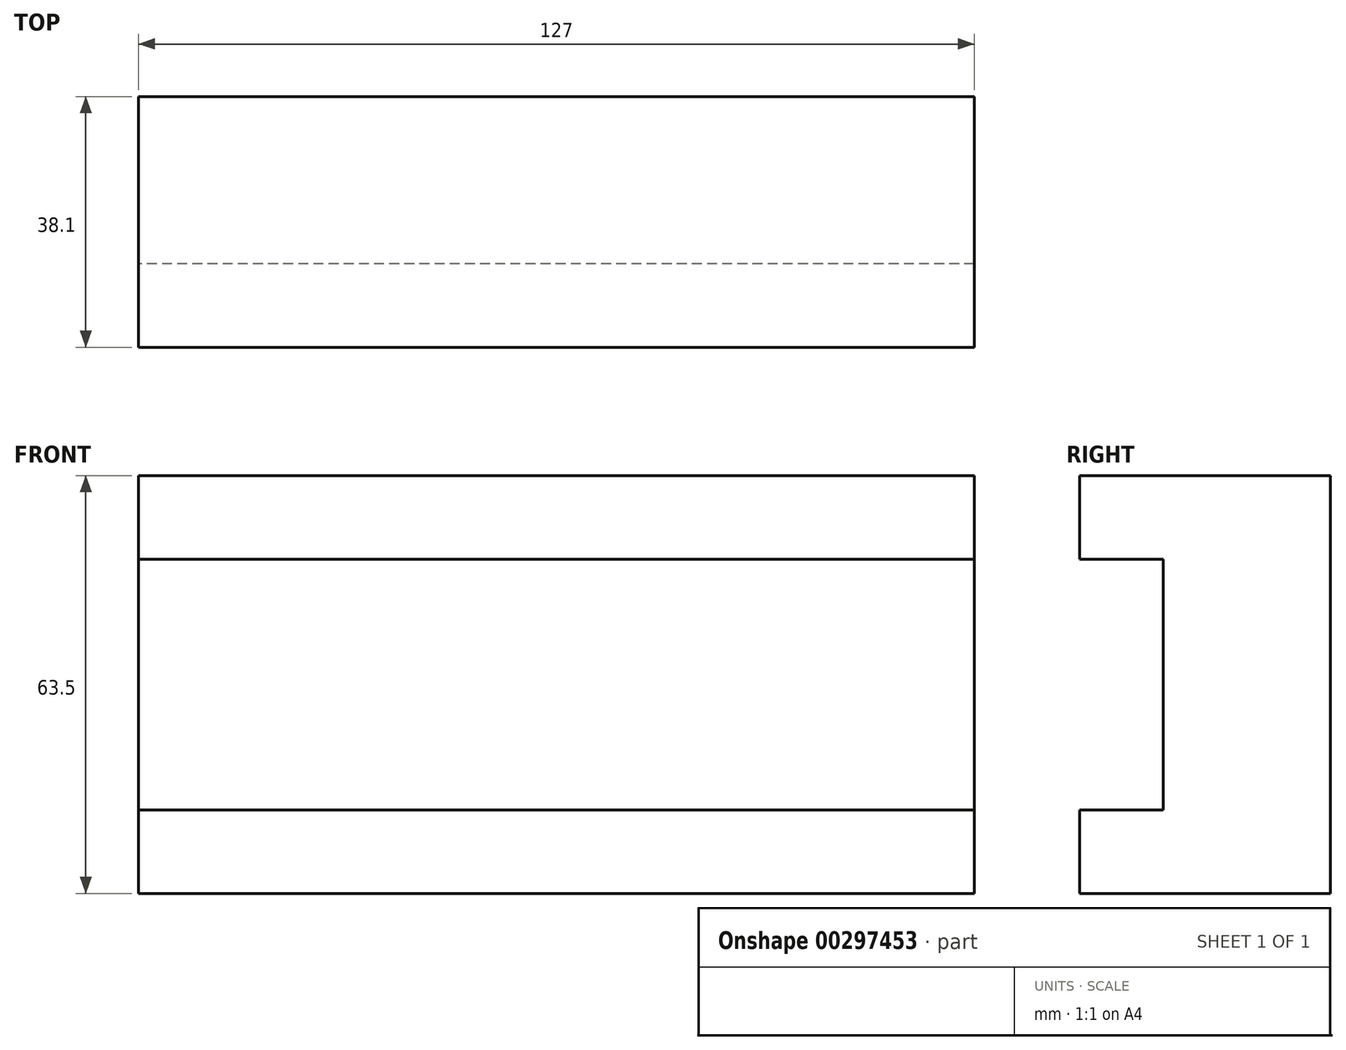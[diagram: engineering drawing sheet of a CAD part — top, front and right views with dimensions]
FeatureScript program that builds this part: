
annotation { "Feature Type Name" : "Feature", "Feature Type Description" : "" }
export const myFeature = defineFeature(function(context is Context, id is Id, definition is map)
    precondition{}
    {
        {
            var Q0;
            Q0=qCreatedBy(makeId("Front.planeOp"),FACE);
            var sketch = newSketch(context, id + "F0", { "sketchPlane" : qUnion([Q0])});
            skLineSegment(sketch, "E0.bottom", {"start": v(63.5, 31.75) * mm, "end": v(-63.5, 31.75) * mm});
            skLineSegment(sketch, "E0.top", {"start": v(63.5, -31.75) * mm, "end": v(-63.5, -31.75) * mm});
            skLineSegment(sketch, "E0.left", {"start": v(63.5, 31.75) * mm, "end": v(63.5, -31.75) * mm});
            skLineSegment(sketch, "E0.right", {"start": v(-63.5, 31.75) * mm, "end": v(-63.5, -31.75) * mm});
            skPoint(sketch, "E0.middle", {"position": v(0, 0) * mm});
            skSolve(sketch);
        }
        {
            var Q0;
            Q0=makeQuery(id+"F0.imprint","IMPRINT",FACE,{"disambiguationData":[TD([[makeQuery(id+"F0.imprint","IMPRINT",EDGE,{"derivedFrom":sQuery(id+"F0.wireOp",EDGE,"E0.bottom")}),1.0]])]});
            extrude(context, id + "F1", {"entities" : qUnion([Q0]), "depth" : 38.1 * mm});
        }
        {
            var Q0;
            Q0=makeQuery(id+"F1.opExtrude","CAP_FACE",FACE,{"disambiguationData":[OSD([sQuery(id+"F0.wireOp",EDGE,"E0.bottom"),sQuery(id+"F0.wireOp",EDGE,"E0.top"),sQuery(id+"F0.wireOp",EDGE,"E0.left"),sQuery(id+"F0.wireOp",EDGE,"E0.right")])],"isStart":false});
            var sketch = newSketch(context, id + "F2", { "sketchPlane" : qUnion([Q0])});
            skLineSegment(sketch, "E1.bottom", {"start": v(63.5, -19.05) * mm, "end": v(-63.5, -19.05) * mm});
            skLineSegment(sketch, "E1.top", {"start": v(63.5, 19.05) * mm, "end": v(-63.5, 19.05) * mm});
            skLineSegment(sketch, "E1.left", {"start": v(63.5, -19.05) * mm, "end": v(63.5, 19.05) * mm});
            skLineSegment(sketch, "E1.right", {"start": v(-63.5, -19.05) * mm, "end": v(-63.5, 19.05) * mm});
            skPoint(sketch, "E1.middle", {"position": v(0, 0) * mm});
            skSolve(sketch);
        }
        {
            var Q0;
            Q0 = qSketchRegion(id + "F2", true);
            extrude(context, id + "F3", {"entities" : qUnion([Q0]), "operationType" : NewBodyOperationType.REMOVE, "oppositeDirection" : true, "depth" : 12.7 * mm});
        }
    });
